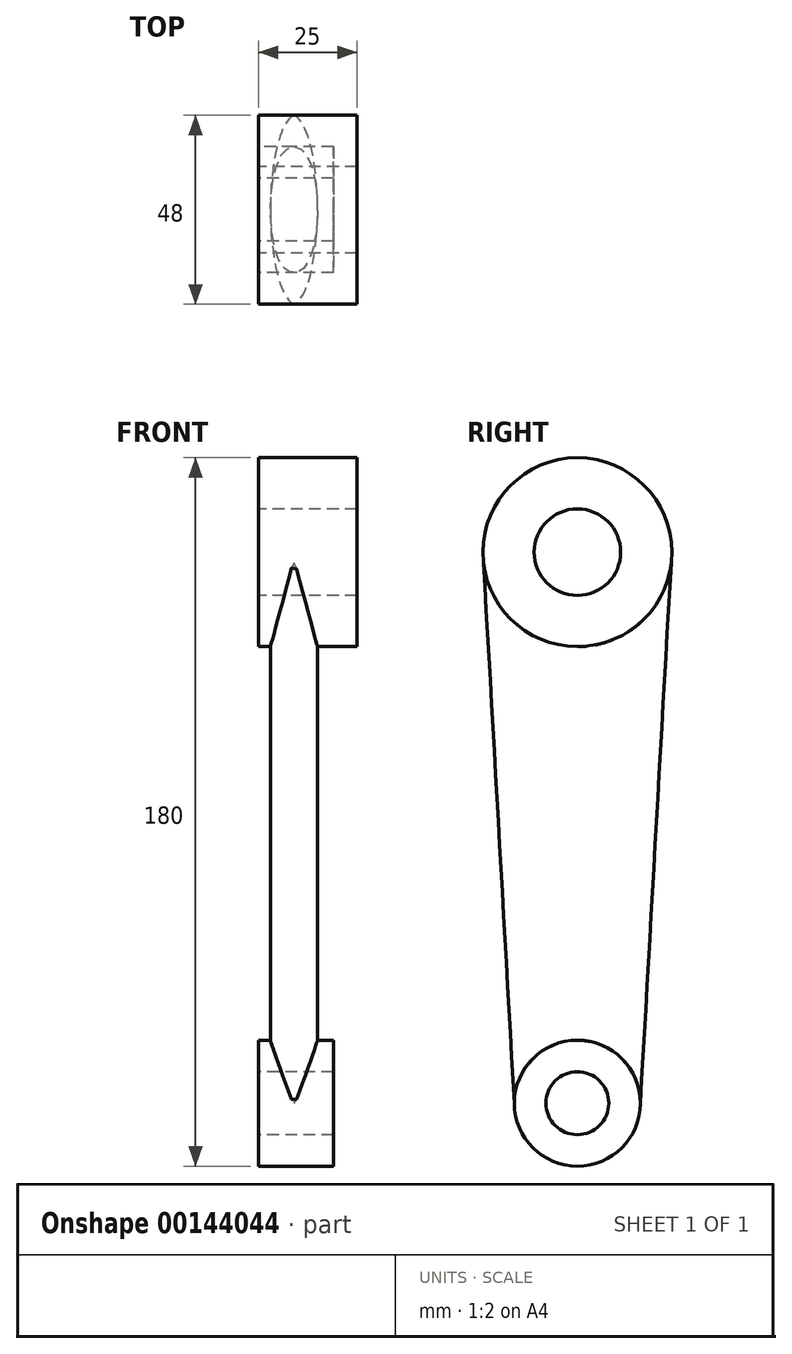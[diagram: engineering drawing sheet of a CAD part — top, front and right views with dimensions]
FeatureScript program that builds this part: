
annotation { "Feature Type Name" : "Feature", "Feature Type Description" : "" }
export const myFeature = defineFeature(function(context is Context, id is Id, definition is map)
    precondition{}
    {
        {
            var Q0;
            Q0=qCreatedBy(makeId("Right.planeOp"),FACE);
            var sketch = newSketch(context, id + "F0", { "sketchPlane" : qUnion([Q0])});
            skCircle(sketch, "E0", {"center": v(0, 0) * mm, "radius": 8 * mm});
            skCircle(sketch, "E1", {"center": v(0, 0) * mm, "radius": 16 * mm});
            skCircle(sketch, "E2", {"center": v(0, 140) * mm, "radius": 24 * mm});
            skCircle(sketch, "E3", {"center": v(0, 140) * mm, "radius": 11 * mm});
            skSolve(sketch);
        }
        {
            var Q0;
            Q0=makeQuery(id+"F0.imprint","IMPRINT",FACE,{"disambiguationData":[TD([[makeQuery(id+"F0.imprint","IMPRINT",EDGE,{"derivedFrom":sQuery(id+"F0.wireOp",EDGE,"E3")}),-1.0]])]});
            extrude(context, id + "F1", {"entities" : qUnion([Q0]), "depth" : 25 * mm});
        }
        {
            var Q0;
            Q0=makeQuery(id+"F0.imprint","IMPRINT",FACE,{"disambiguationData":[TD([[makeQuery(id+"F0.imprint","IMPRINT",EDGE,{"derivedFrom":sQuery(id+"F0.wireOp",EDGE,"E0")}),-1.0]])]});
            extrude(context, id + "F2", {"entities" : qUnion([Q0]), "depth" : 19 * mm});
        }
        {
            var Q0;
            Q0=qCreatedBy(makeId("Top.planeOp"),FACE);
            var sketch = newSketch(context, id + "F3", { "sketchPlane" : qUnion([Q0])});
            skEllipse(sketch, "E4", {"center": v(9, 0) * mm, "majorRadius": 16 * mm, "minorRadius": 6 * mm, "majorAxis": v(0, 1)});
            skPoint(sketch, "E5", {"position": v(3, 0) * mm});
            skPoint(sketch, "E6", {"position": v(0, 0) * mm});
            skLineSegment(sketch, "E7.0", {"start": v(0, 11) * mm, "end": v(0, -11) * mm, "construction": true});
            skLineSegment(sketch, "E8", {"start": v(0, 16) * mm, "end": v(19, 16) * mm, "construction": true});
            skLineSegment(sketch, "E9.0", {"start": v(19, 16) * mm, "end": v(19, -16) * mm, "construction": true});
            skLineSegment(sketch, "E10", {"start": v(19, -16) * mm, "end": v(0, -16) * mm, "construction": true});
            skLineSegment(sketch, "E11.0", {"start": v(0, 24) * mm, "end": v(0, -24) * mm, "construction": true});
            skSolve(sketch);
        }
        {
            var Q0;
            Q0=sQuery(id+"F0.wireOp",VERTEX,"E2.center");
            var Q1;
            Q1=qCreatedBy(makeId("Top.planeOp"),FACE);
            cPlane(context, id + "F4", {"entities" : qUnion([Q0, Q1]), "cplaneType" : CPlaneType.PLANE_POINT, "offset" : 25 * mm, "width" : 150 * mm, "height" : 150 * mm});
        }
        {
            var Q0;
            Q0=qCreatedBy(id+"F4.planeOp",FACE);
            var sketch = newSketch(context, id + "F5", { "sketchPlane" : qUnion([Q0])});
            skLineSegment(sketch, "E12.0", {"start": v(0, 24) * mm, "end": v(0, -24) * mm, "construction": true});
            skLineSegment(sketch, "E13", {"start": v(25, -24) * mm, "end": v(0, -24) * mm, "construction": true});
            skLineSegment(sketch, "E14.0", {"start": v(25, 24) * mm, "end": v(25, -24) * mm, "construction": true});
            skLineSegment(sketch, "E15", {"start": v(0, 24) * mm, "end": v(25, 24) * mm, "construction": true});
            skEllipse(sketch, "E16", {"center": v(9, 0) * mm, "majorRadius": 24 * mm, "minorRadius": 6 * mm, "majorAxis": v(0, 1)});
            skPoint(sketch, "E17", {"position": v(3, 0) * mm});
            skSolve(sketch);
        }
        {
            var Q0;
            Q0 = qSketchRegion(id + "F5", true);
            var Q1;
            Q1 = qSketchRegion(id + "F3", true);
            loft(context, id + "F6", {"operationType" : NewBodyOperationType.ADD, "sheetProfilesArray" : [{ "sheetProfileEntities" : qUnion([Q0]) }, { "sheetProfileEntities" : qUnion([Q1]) }]});
        }
        {
            var Q0;
            Q0=makeQuery(id+"F0.imprint","IMPRINT",FACE,{"disambiguationData":[TD([[makeQuery(id+"F0.imprint","IMPRINT",EDGE,{"derivedFrom":sQuery(id+"F0.wireOp",EDGE,"E3")}),1.0]])]});
            var Q1;
            Q1=makeQuery(id+"F0.imprint","IMPRINT",FACE,{"disambiguationData":[TD([[makeQuery(id+"F0.imprint","IMPRINT",EDGE,{"derivedFrom":sQuery(id+"F0.wireOp",EDGE,"E0")}),1.0]])]});
            extrude(context, id + "F7", {"entities" : qUnion([Q0, Q1]), "operationType" : NewBodyOperationType.REMOVE, "depth" : 25 * mm});
        }
    });
